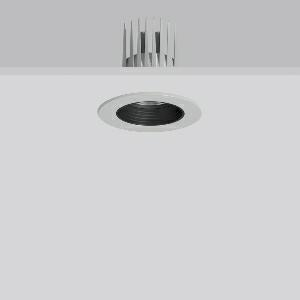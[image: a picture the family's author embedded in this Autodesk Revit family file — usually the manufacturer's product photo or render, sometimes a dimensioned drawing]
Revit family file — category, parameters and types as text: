
# Revit family: heledon_mini_e_901754_004_3_88b5
name_source: partatom
category: Lighting Fixtures
units: mm (PartAtom-declared; Revit-internal decimal feet)

## family parameters
Cut with Voids When Loaded = No
Host = Face
Light Source = No
Part Type = Normal
Room Calculation Point = No
Round Connector Dimension = Use Diameter
Shared = No

## types (1)
- HELEDON mini E (1 x LED Modul 935, 3300 lm, 3500)
    Apparent Load = 29 VA
    Approval mark = CE
    CIE Flux Codes = 80 99 100 100 100
    Color Rendering = 92
    Color Temperature = 3500
    Default Elevation = 1800 mm
    Description = Series: HELEDON mini
Round recessed downlight. Housing: die-cast aluminium, powder-coated. Black plastic ring and recessed LED to prevent glare from the side. Optical assembly with lens made of plastic (polycarbonate) for the best homogeneous light distribution - can be changed without tools. Best colour rendering index Ra>90. Suitable for Recessed ceiling mounting. Installation without tools thanks to spring fastening system. Including separate LED converter with connecting cable 600 mm.High quality converter without flickering and stroboscopic effect. Through-wiring box (5 pole) available as accessory. The following accessories can be mounted without use of tools: interchangeable lenses, decorative glasses, honeycomb louvre, clear and frosted diffusers, white interchangeable plastic ring. 
Colour: silver
Diameter: 124 mm
Height: 3 mm
Cut-out diameter: 114 mm
Recess height: 170 mm
Luminaire: recess height: 120 mm
Lamp: LED
Socket: without socket
Colour temperature: 3500K
Colour rendering index (CRI): 92
System power: 29 W
Rated luminous flux: 3300 lm
Luminous efficiency: 114 lm/W
Control gear: Regulated power supply
Protection class: II
Type of protection: IP 20
    Height = 0 mm  [stored 0 ft]
    Lamp = 1 x LED Modul 935
    Lamp Light Flux = 3300 lm
    Lamp count = 1
    Length = 124 mm  [stored 0.406824 ft]
    Lifetime = 50000 h
    Luminous efficacy = 114 lm/W
    Manufacturer = RZB
    ModVariant = No
    Model = 901754.004.3
    Mounting Place = Ceiling
    Mounting Type = Recessed
    Number of Poles = 1
    OnlyDefault = Yes
    Power Factor = 1
    Product Name = HELEDON mini E
    Product group = Recessed downlights
    ProductGroupID = 402
    Protection Class = Protection class II
    Protection Degree = IP 20
    RLX_Detail_Level = 1
    RLX_Emergency_Light_Flux = 0 lm
    RLX_Emergency_Type = 0
    RLX_Emergency_Type_DB = No
    RlxData = <blob elided: 124681 chars, md5=a88a1288>
    Socket = socket
    Standby Power = 0 W
    System Light Flux = 3300 lm
    System Power = 29 W
    Type Comments = Product without accessories
    Type Image = 901656.004.jpg
    URL = http://relux.com
    VarID = ---
    Voltage = 230 V
    Voltage Range = 220-240 V
    Weight = 0.00 kg
    Width = 0 mm  [stored 0 ft]

note: [stored X ft] marks values corroborated as IEEE doubles in the binary element streams (Revit-internal decimal feet)

## geometry (parser evidence)
native form markers: Blend x4, Sweep x11
no freeform markers — native parametric forms only
